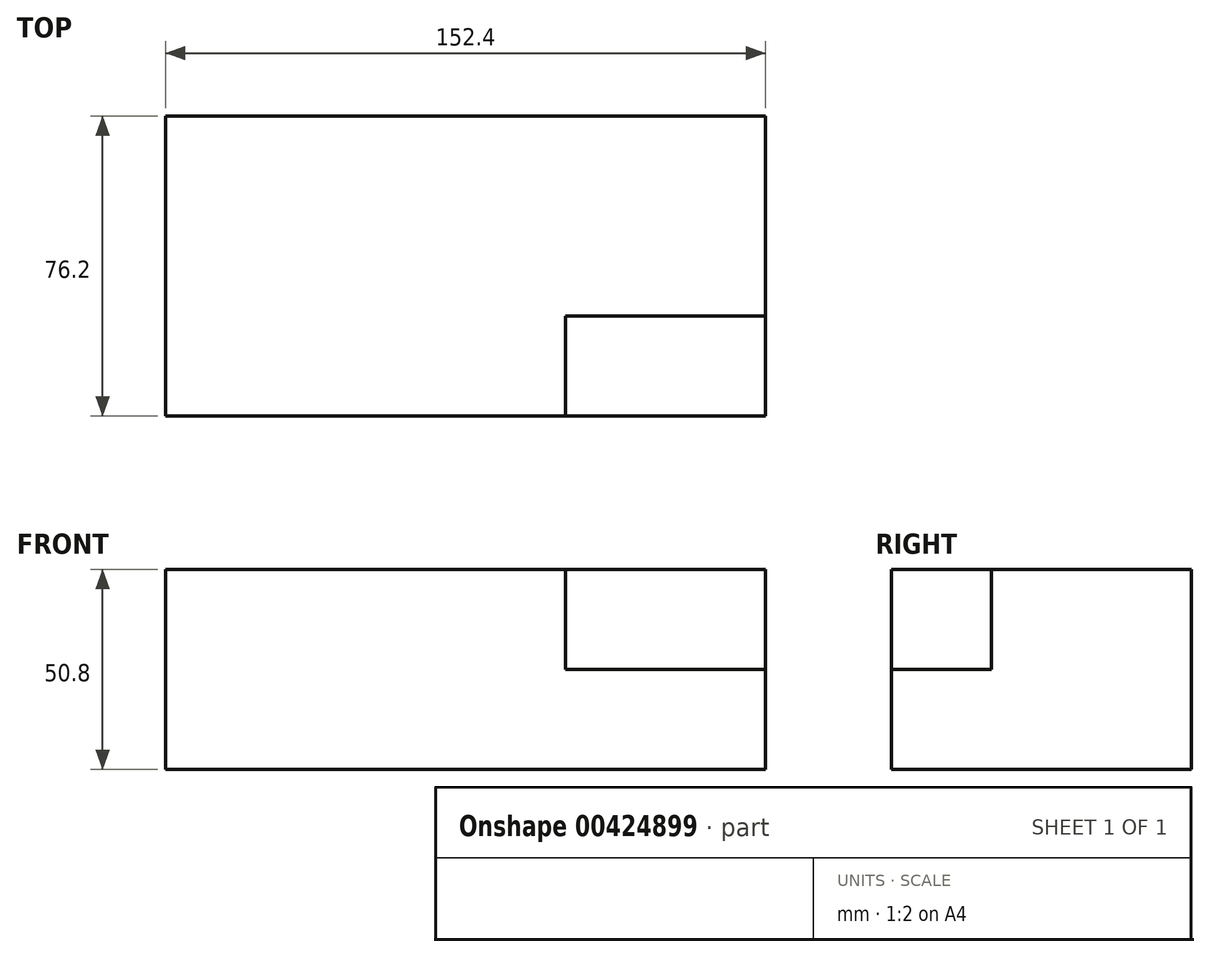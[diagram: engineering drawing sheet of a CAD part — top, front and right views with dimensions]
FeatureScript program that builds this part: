
annotation { "Feature Type Name" : "Feature", "Feature Type Description" : "" }
export const myFeature = defineFeature(function(context is Context, id is Id, definition is map)
    precondition{}
    {
        {
            var Q0;
            Q0=qCreatedBy(makeId("Top.planeOp"),FACE);
            var sketch = newSketch(context, id + "F0", { "sketchPlane" : qUnion([Q0])});
            skLineSegment(sketch, "E0", {"start": v(0, 0) * mm, "end": v(152.4, 0) * mm});
            skLineSegment(sketch, "E1", {"start": v(152.4, 0) * mm, "end": v(152.4, 76.2) * mm});
            skLineSegment(sketch, "E2", {"start": v(152.4, 76.2) * mm, "end": v(0, 76.2) * mm});
            skLineSegment(sketch, "E3", {"start": v(0, 76.2) * mm, "end": v(0, 0) * mm});
            skSolve(sketch);
        }
        {
            var Q0;
            Q0=makeQuery(id+"F0.imprint","IMPRINT",FACE,{"disambiguationData":[TD([[makeQuery(id+"F0.imprint","IMPRINT",EDGE,{"derivedFrom":sQuery(id+"F0.wireOp",EDGE,"E0")}),1.0]])]});
            extrude(context, id + "F1", {"entities" : qUnion([Q0]), "depth" : 50.8 * mm});
        }
        {
            var Q0;
            Q0=makeQuery(id+"F1.opExtrude","SWEPT_FACE",FACE,{"disambiguationData":[OSD([sQuery(id+"F0.wireOp",EDGE,"E0")])]});
            var sketch = newSketch(context, id + "F2", { "sketchPlane" : qUnion([Q0])});
            skLineSegment(sketch, "E4", {"start": v(152.4, 50.8) * mm, "end": v(101.6, 50.8) * mm});
            skLineSegment(sketch, "E5", {"start": v(101.6, 50.8) * mm, "end": v(101.6, 25.4) * mm});
            skLineSegment(sketch, "E6", {"start": v(101.6, 25.4) * mm, "end": v(152.4, 25.4) * mm});
            skLineSegment(sketch, "E7", {"start": v(152.4, 25.4) * mm, "end": v(152.4, 50.8) * mm});
            skSolve(sketch);
        }
        {
            var Q0;
            Q0=makeQuery(id+"F2.imprint","IMPRINT",FACE,{"disambiguationData":[TD([[makeQuery(id+"F2.imprint","IMPRINT",EDGE,{"derivedFrom":sQuery(id+"F2.wireOp",EDGE,"E4")}),-1.0]])]});
            extrude(context, id + "F3", {"entities" : qUnion([Q0]), "operationType" : NewBodyOperationType.REMOVE, "oppositeDirection" : true, "depth" : 25.4 * mm});
        }
    });
